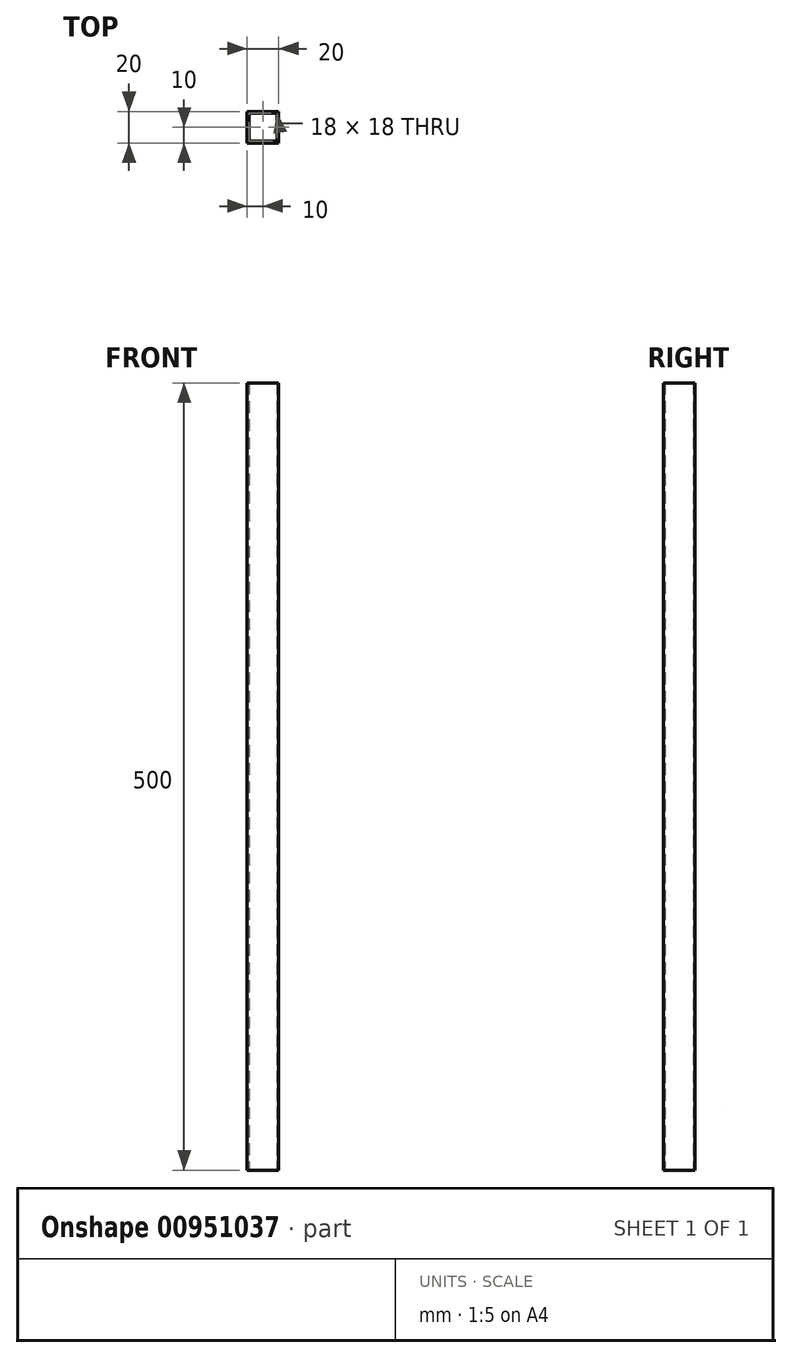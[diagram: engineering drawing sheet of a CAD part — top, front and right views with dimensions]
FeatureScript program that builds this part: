
annotation { "Feature Type Name" : "Feature", "Feature Type Description" : "" }
export const myFeature = defineFeature(function(context is Context, id is Id, definition is map)
    precondition{}
    {
        {
            var Q0;
            Q0=qCreatedBy(makeId("Top.planeOp"),FACE);
            var sketch = newSketch(context, id + "F0", { "sketchPlane" : qUnion([Q0])});
            skLineSegment(sketch, "E0.bottom", {"start": v(10, 10) * mm, "end": v(-10, 10) * mm});
            skLineSegment(sketch, "E0.top", {"start": v(10, -10) * mm, "end": v(-10, -10) * mm});
            skLineSegment(sketch, "E0.left", {"start": v(10, 10) * mm, "end": v(10, -10) * mm});
            skLineSegment(sketch, "E0.right", {"start": v(-10, 10) * mm, "end": v(-10, -10) * mm});
            skPoint(sketch, "E0.middle", {"position": v(0, 0) * mm});
            skLineSegment(sketch, "E1.bottom", {"start": v(9, 9) * mm, "end": v(-9, 9) * mm});
            skLineSegment(sketch, "E1.top", {"start": v(9, -9) * mm, "end": v(-9, -9) * mm});
            skLineSegment(sketch, "E1.left", {"start": v(9, 9) * mm, "end": v(9, -9) * mm});
            skLineSegment(sketch, "E1.right", {"start": v(-9, 9) * mm, "end": v(-9, -9) * mm});
            skSolve(sketch);
        }
        {
            var Q0;
            Q0=makeQuery(id+"F0.imprint","IMPRINT",FACE,{"disambiguationData":[TD([[makeQuery(id+"F0.imprint","IMPRINT",EDGE,{"derivedFrom":sQuery(id+"F0.wireOp",EDGE,"E0.bottom")}),1.0]])]});
            extrude(context, id + "F1", {"entities" : qUnion([Q0]), "depth" : 500 * mm, "offsetDistance" : 25 * mm});
        }
    });
